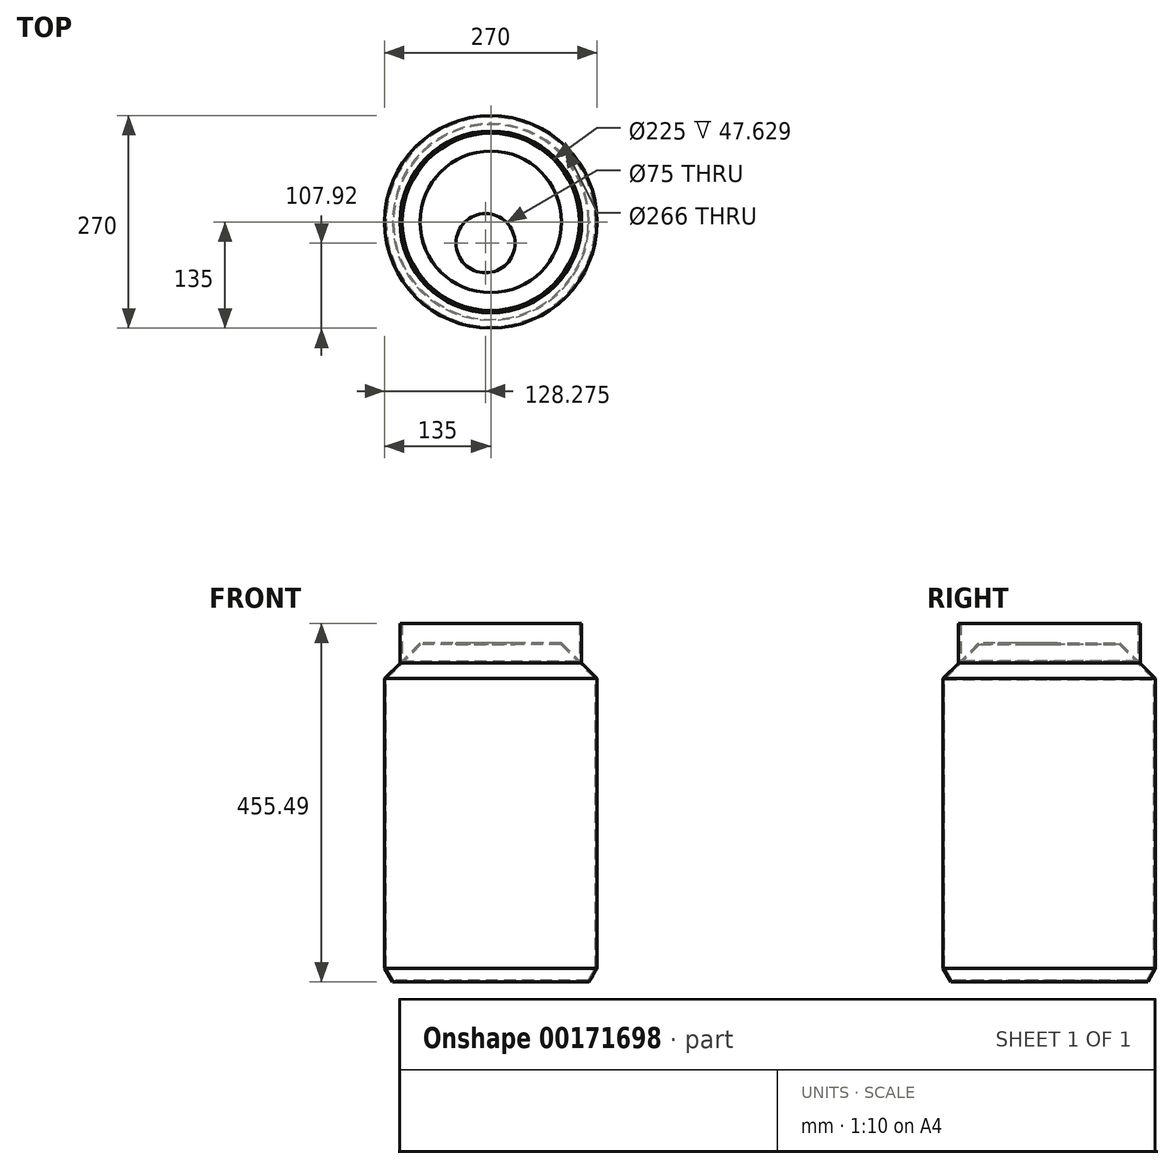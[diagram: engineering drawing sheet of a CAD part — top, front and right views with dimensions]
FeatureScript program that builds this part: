
annotation { "Feature Type Name" : "Feature", "Feature Type Description" : "" }
export const myFeature = defineFeature(function(context is Context, id is Id, definition is map)
    precondition{}
    {
        {
            var Q0;
            Q0=qCreatedBy(makeId("Front.planeOp"),FACE);
            var sketch = newSketch(context, id + "F0", { "sketchPlane" : qUnion([Q0])});
            skLineSegment(sketch, "E0", {"start": v(0, 296.43) * mm, "end": v(0, -71.57) * mm});
            skLineSegment(sketch, "E1", {"start": v(-45.13, 341.56) * mm, "end": v(0, 296.43) * mm});
            skLineSegment(sketch, "E2", {"start": v(-10.02, -88.93) * mm, "end": v(0, -71.57) * mm});
            skPoint(sketch, "E3.orphan", {"position": v(0, -109.38) * mm});
            skPoint(sketch, "E4.orphan", {"position": v(0, 110.31) * mm});
            skLineSegment(sketch, "E5", {"start": v(-45.13, 341.56) * mm, "end": v(-135, 341.56) * mm});
            skLineSegment(sketch, "E6", {"start": v(-10.02, -88.93) * mm, "end": v(-135, -88.93) * mm});
            skLineSegment(sketch, "E7.0", {"start": v(-11.18, -86.93) * mm, "end": v(-135, -86.93) * mm});
            skLineSegment(sketch, "E7.1", {"start": v(-45.96, 339.56) * mm, "end": v(-135, 339.56) * mm});
            skLineSegment(sketch, "E7.2", {"start": v(-45.96, 339.56) * mm, "end": v(-2, 295.6) * mm});
            skLineSegment(sketch, "E7.3", {"start": v(-2, 295.6) * mm, "end": v(-2, -71.04) * mm});
            skLineSegment(sketch, "E7.4", {"start": v(-11.18, -86.93) * mm, "end": v(-2, -71.04) * mm});
            skLineSegment(sketch, "E8", {"start": v(-135, 341.56) * mm, "end": v(-135, -88.93) * mm});
            skSolve(sketch);
        }
        {
            var Q0;
            Q0=makeQuery(id+"F0.imprint","IMPRINT",FACE,{"disambiguationData":[TD([[makeQuery(id+"F0.imprint","IMPRINT",EDGE,{"derivedFrom":sQuery(id+"F0.wireOp",EDGE,"E0")}),-1.0]])]});
            var Q1;
            Q1=sQuery(id+"F0.wireOp",EDGE,"E8");
            revolve(context, id + "F1", {"entities" : qUnion([Q0]), "axis" : qUnion([Q1]), "revolveType" : RevolveType.FULL});
        }
        {
            var Q0;
            Q0=makeQuery(id+"F1.opRevolve","SWEPT_FACE",FACE,{"disambiguationData":[OSD([sQuery(id+"F0.wireOp",EDGE,"E5")])]});
            var sketch = newSketch(context, id + "F4", { "sketchPlane" : qUnion([Q0])});
            skCircle(sketch, "E9", {"center": v(-135, 0) * mm, "radius": 112.5 * mm});
            skCircle(sketch, "E10.0", {"center": v(-135, 0) * mm, "radius": 115.5 * mm});
            skSolve(sketch);
        }
        {
            var Q0;
            Q0=makeQuery(id+"F4.imprint","IMPRINT",FACE,{"disambiguationData":[TD([[makeQuery(id+"F4.imprint","IMPRINT",EDGE,{"derivedFrom":sQuery(id+"F4.wireOp",EDGE,"E9")}),-1.0]])]});
            extrude(context, id + "F2", {"entities" : qUnion([Q0]), "operationType" : NewBodyOperationType.ADD, "endBound" : BoundingType.SYMMETRIC, "depth" : 50 * mm});
        }
        {
            var Q0;
            Q0=makeQuery(id+"F1.opRevolve","SWEPT_FACE",FACE,{"disambiguationData":[OSD([sQuery(id+"F0.wireOp",EDGE,"E5")])]});
            var sketch = newSketch(context, id + "F3", { "sketchPlane" : qUnion([Q0])});
            skCircle(sketch, "E11", {"center": v(-141.73, -27.08) * mm, "radius": 37.5 * mm});
            skSolve(sketch);
        }
        {
            var Q0;
            Q0=makeQuery(id+"F3.imprint","IMPRINT",FACE,{"disambiguationData":[TD([[makeQuery(id+"F3.imprint","IMPRINT",EDGE,{"derivedFrom":sQuery(id+"F3.wireOp",EDGE,"E11")}),1.0]])]});
            extrude(context, id + "F5", {"entities" : qUnion([Q0]), "operationType" : NewBodyOperationType.REMOVE, "endBound" : BoundingType.UP_TO_NEXT, "oppositeDirection" : true, "depth" : 25 * mm});
        }
    });
